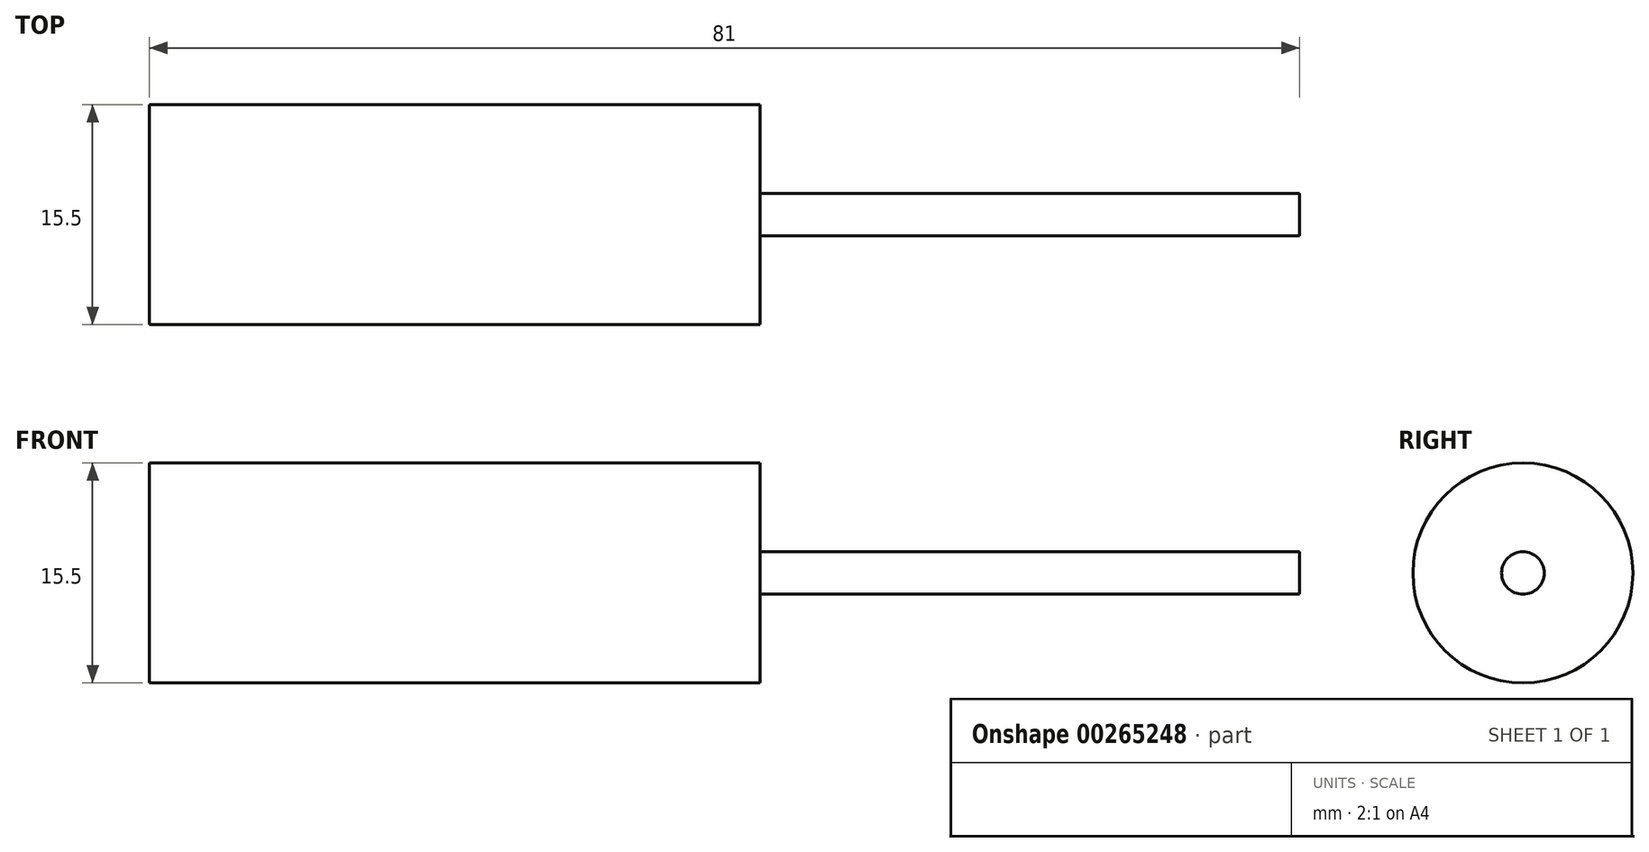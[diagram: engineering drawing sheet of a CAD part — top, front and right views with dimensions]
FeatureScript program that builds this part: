
annotation { "Feature Type Name" : "Feature", "Feature Type Description" : "" }
export const myFeature = defineFeature(function(context is Context, id is Id, definition is map)
    precondition{}
    {
        {
            var Q0;
            Q0=qCreatedBy(makeId("Right.planeOp"),FACE);
            var sketch = newSketch(context, id + "F0", { "sketchPlane" : qUnion([Q0])});
            skCircle(sketch, "E0", {"center": v(0, 0) * mm, "radius": 7.75 * mm});
            skCircle(sketch, "E1", {"center": v(0, 0) * mm, "radius": 1.5 * mm});
            skSolve(sketch);
        }
        {
            var Q0;
            Q0 = qSketchRegion(id + "F0", true);
            extrude(context, id + "F1", {"entities" : qUnion([Q0]), "depth" : 43 * mm});
        }
        {
            var Q0;
            Q0=qCreatedBy(makeId("Right.planeOp"),FACE);
            var sketch = newSketch(context, id + "F2", { "sketchPlane" : qUnion([Q0])});
            skCircle(sketch, "E2", {"center": v(0, 0) * mm, "radius": 1.5 * mm});
            skSolve(sketch);
        }
        {
            var Q0;
            Q0 = qSketchRegion(id + "F2", true);
            extrude(context, id + "F3", {"entities" : qUnion([Q0]), "operationType" : NewBodyOperationType.ADD, "depth" : 81 * mm});
        }
    });
